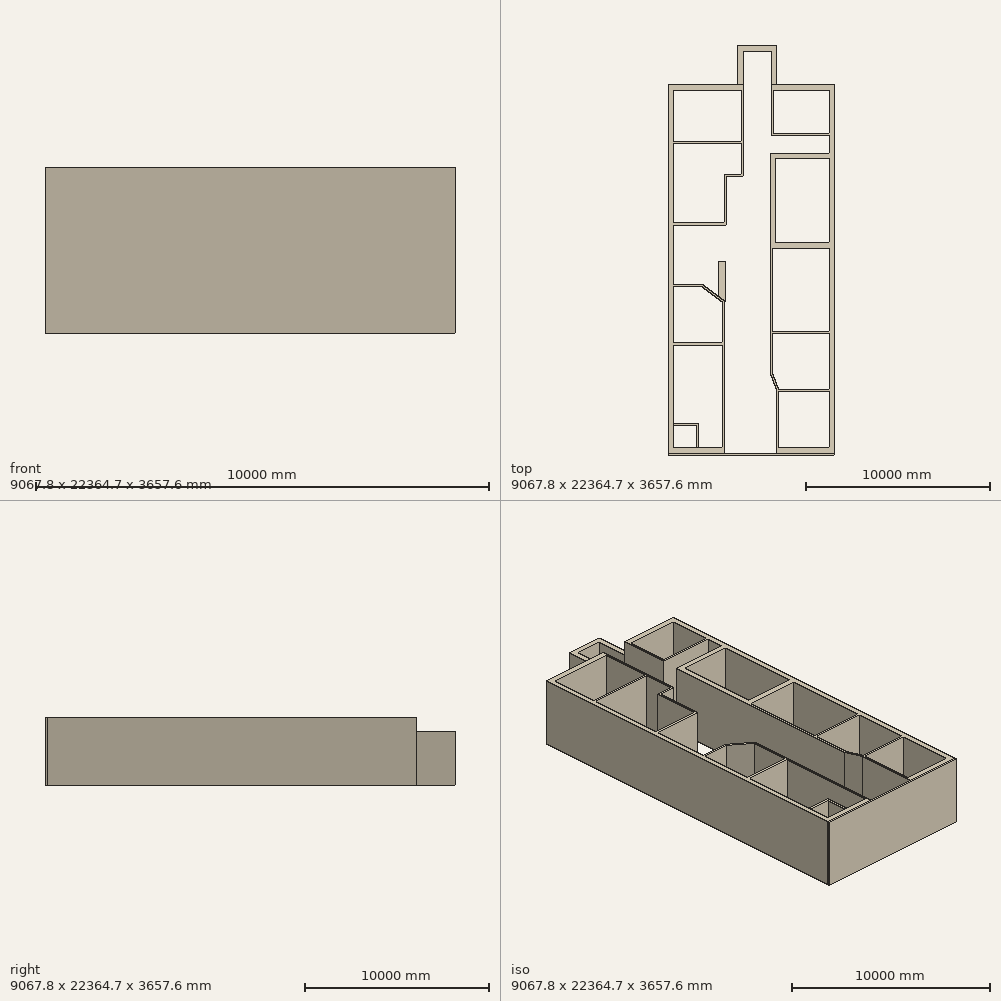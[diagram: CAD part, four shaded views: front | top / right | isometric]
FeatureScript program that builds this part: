
annotation { "Feature Type Name" : "Feature", "Feature Type Description" : "" }
export const myFeature = defineFeature(function(context is Context, id is Id, definition is map)
    precondition{}
    {
        {
            var Q0;
            Q0=qCreatedBy(makeId("Top.planeOp"),FACE);
            var sketch = newSketch(context, id + "F0", { "sketchPlane" : qUnion([Q0])});
            skLineSegment(sketch, "E0.bottom", {"start": v(1936.55, -1664.77) * mm, "end": v(-806.65, -1664.77) * mm});
            skLineSegment(sketch, "E0.top", {"start": v(1936.55, 1383.23) * mm, "end": v(-806.65, 1383.23) * mm});
            skLineSegment(sketch, "E0.left", {"start": v(1936.55, -1664.77) * mm, "end": v(1936.55, 1383.23) * mm});
            skLineSegment(sketch, "E0.right", {"start": v(-806.65, -1664.77) * mm, "end": v(-806.65, 1383.23) * mm});
            skLineSegment(sketch, "E1.0", {"start": v(-920.95, -1969.57) * mm, "end": v(-920.95, 1476.8) * mm});
            skLineSegment(sketch, "E1.1", {"start": v(1936.55, 1497.53) * mm, "end": v(-806.65, 1497.53) * mm});
            skLineSegment(sketch, "E2.1", {"start": v(2241.35, -1969.57) * mm, "end": v(-920.95, -1969.57) * mm});
            skLineSegment(sketch, "E3.0", {"start": v(1936.55, 4545.53) * mm, "end": v(-1149.55, 4545.53) * mm});
            skLineSegment(sketch, "E4", {"start": v(1936.55, 4545.53) * mm, "end": v(1936.55, 1497.53) * mm});
            skLineSegment(sketch, "E5.0", {"start": v(1936.55, 4659.83) * mm, "end": v(-1149.55, 4659.83) * mm});
            skLineSegment(sketch, "E6", {"start": v(-920.95, -1969.57) * mm, "end": v(-3740.35, -1969.57) * mm});
            skLineSegment(sketch, "E7.0", {"start": v(1936.55, 9536.63) * mm, "end": v(-959.05, 9536.63) * mm});
            skLineSegment(sketch, "E8.0", {"start": v(1936.55, 9231.83) * mm, "end": v(-1149.55, 9231.83) * mm});
            skLineSegment(sketch, "E8.1", {"start": v(-1149.55, 4659.83) * mm, "end": v(-1149.55, 9231.83) * mm});
            skLineSegment(sketch, "E9", {"start": v(1936.55, 4659.83) * mm, "end": v(1936.55, 9231.83) * mm});
            skLineSegment(sketch, "E10", {"start": v(2241.35, 9536.63) * mm, "end": v(2241.35, -1969.57) * mm});
            skLineSegment(sketch, "E11.0", {"start": v(1936.55, 14108.63) * mm, "end": v(-959.05, 14108.63) * mm});
            skLineSegment(sketch, "E12.0", {"start": v(1936.55, 14413.43) * mm, "end": v(-1263.85, 14413.43) * mm});
            skLineSegment(sketch, "E13", {"start": v(2241.35, 9536.63) * mm, "end": v(2241.35, 18147.23) * mm});
            skLineSegment(sketch, "E14", {"start": v(1936.55, 9536.63) * mm, "end": v(1936.55, 14108.63) * mm});
            skLineSegment(sketch, "E15", {"start": v(-1263.85, 14413.43) * mm, "end": v(-1263.85, 2391.2) * mm});
            skLineSegment(sketch, "E16.0", {"start": v(-959.05, 14108.63) * mm, "end": v(-959.05, 9536.63) * mm});
            skLineSegment(sketch, "E17", {"start": v(1936.55, 14413.43) * mm, "end": v(1936.55, 15365.93) * mm});
            skLineSegment(sketch, "E18", {"start": v(1936.55, 15365.93) * mm, "end": v(-1225.75, 15365.93) * mm});
            skLineSegment(sketch, "E19.0", {"start": v(1936.55, 17842.43) * mm, "end": v(-1111.45, 17842.43) * mm});
            skLineSegment(sketch, "E20", {"start": v(1936.55, 15480.23) * mm, "end": v(1936.55, 17842.43) * mm});
            skLineSegment(sketch, "E21.0", {"start": v(2241.35, 18147.23) * mm, "end": v(-1225.75, 18147.23) * mm});
            skLineSegment(sketch, "E22.0", {"start": v(-1111.45, 17842.43) * mm, "end": v(-1111.45, 15480.23) * mm});
            skLineSegment(sketch, "E23", {"start": v(-1111.45, 15480.23) * mm, "end": v(1936.55, 15480.23) * mm});
            skLineSegment(sketch, "E24", {"start": v(-1225.75, 15365.93) * mm, "end": v(-1225.75, 18147.23) * mm});
            skLineSegment(sketch, "E25.0", {"start": v(-2749.75, 13118.03) * mm, "end": v(-2749.75, 18147.23) * mm});
            skLineSegment(sketch, "E26.0", {"start": v(-2864.05, 15061.13) * mm, "end": v(-2864.05, 17842.43) * mm});
            skLineSegment(sketch, "E27.0", {"start": v(-6521.65, 15061.13) * mm, "end": v(-6521.65, 17842.43) * mm});
            skLineSegment(sketch, "E28", {"start": v(-2749.75, 18147.23) * mm, "end": v(-6826.45, 18147.23) * mm});
            skLineSegment(sketch, "E29.0", {"start": v(-2864.05, 17842.43) * mm, "end": v(-6521.65, 17842.43) * mm});
            skLineSegment(sketch, "E30.0", {"start": v(-6826.45, -1969.57) * mm, "end": v(-6826.45, 18147.23) * mm});
            skLineSegment(sketch, "E31.0", {"start": v(-2864.05, 15061.13) * mm, "end": v(-6521.65, 15061.13) * mm});
            skLineSegment(sketch, "E32.0", {"start": v(-2864.05, 14946.83) * mm, "end": v(-6521.65, 14946.83) * mm});
            skLineSegment(sketch, "E33.0", {"start": v(-3778.45, 10603.43) * mm, "end": v(-6521.65, 10603.43) * mm});
            skLineSegment(sketch, "E34", {"start": v(-6521.65, 14946.83) * mm, "end": v(-6521.65, 10603.43) * mm});
            skLineSegment(sketch, "E35.0", {"start": v(-3778.45, 13232.33) * mm, "end": v(-3778.45, 10603.43) * mm});
            skLineSegment(sketch, "E36.0", {"start": v(-2749.75, 13118.03) * mm, "end": v(-3664.15, 13118.03) * mm});
            skLineSegment(sketch, "E37", {"start": v(-2864.05, 14946.83) * mm, "end": v(-2864.05, 13232.33) * mm});
            skLineSegment(sketch, "E38.0", {"start": v(-2864.05, 13232.33) * mm, "end": v(-3778.45, 13232.33) * mm});
            skLineSegment(sketch, "E39.0", {"start": v(-3664.15, 13118.03) * mm, "end": v(-3664.15, 10489.13) * mm});
            skLineSegment(sketch, "E40.0", {"start": v(-3664.15, 10489.13) * mm, "end": v(-6521.65, 10489.13) * mm});
            skLineSegment(sketch, "E41.0", {"start": v(-4959.55, 7237.93) * mm, "end": v(-6521.65, 7237.93) * mm});
            skLineSegment(sketch, "E42", {"start": v(-6521.65, 7123.63) * mm, "end": v(-6521.65, -1664.77) * mm});
            skLineSegment(sketch, "E43.0", {"start": v(-4997.65, 7123.63) * mm, "end": v(-6521.65, 7123.63) * mm});
            skLineSegment(sketch, "E44", {"start": v(-1149.55, 2411.93) * mm, "end": v(-1149.55, 4545.53) * mm});
            skLineSegment(sketch, "E45", {"start": v(-6826.45, -1969.57) * mm, "end": v(-3740.35, -1969.57) * mm});
            skLineSegment(sketch, "E46", {"start": v(-6521.65, 10489.13) * mm, "end": v(-6521.65, 7237.93) * mm});
            skLineSegment(sketch, "E47", {"start": v(-3740.35, 6323.53) * mm, "end": v(-3740.35, -1969.57) * mm});
            skLineSegment(sketch, "E48.0", {"start": v(-3854.65, 6266.38) * mm, "end": v(-3854.65, -1664.77) * mm});
            skLineSegment(sketch, "E49", {"start": v(-806.65, 1497.53) * mm, "end": v(-1149.55, 2411.93) * mm});
            skLineSegment(sketch, "E50.0", {"start": v(-920.95, 1476.8) * mm, "end": v(-1263.85, 2391.2) * mm});
            skPoint(sketch, "E51.orphan", {"position": v(-1263.85, 2587.67) * mm});
            skLineSegment(sketch, "E52.0", {"start": v(-6521.65, -1664.77) * mm, "end": v(-3854.65, -1664.77) * mm});
            skLineSegment(sketch, "E53", {"start": v(-2749.75, 18147.23) * mm, "end": v(-1225.75, 18147.23) * mm});
            skLineSegment(sketch, "E54.bottom", {"start": v(-2749.75, 19976.03) * mm, "end": v(-1225.75, 19976.03) * mm});
            skLineSegment(sketch, "E54.left", {"start": v(-2749.75, 19976.03) * mm, "end": v(-2749.75, 18147.23) * mm});
            skLineSegment(sketch, "E54.right", {"start": v(-1225.75, 19976.03) * mm, "end": v(-1225.75, 18147.23) * mm});
            skLineSegment(sketch, "E55.0", {"start": v(-3054.55, 20280.83) * mm, "end": v(-3054.55, 18147.23) * mm});
            skLineSegment(sketch, "E55.1", {"start": v(-3054.55, 20280.83) * mm, "end": v(-920.95, 20280.83) * mm});
            skLineSegment(sketch, "E55.2", {"start": v(-920.95, 20280.83) * mm, "end": v(-920.95, 18147.23) * mm});
            skLineSegment(sketch, "E56.0", {"start": v(-920.95, -1855.27) * mm, "end": v(-3740.35, -1855.27) * mm});
            skLineSegment(sketch, "E57.0", {"start": v(-920.95, -636.07) * mm, "end": v(-3740.35, -636.07) * mm});
            skLineSegment(sketch, "E58.0", {"start": v(-920.95, -750.37) * mm, "end": v(-3740.35, -750.37) * mm});
            skLineSegment(sketch, "E59", {"start": v(-3740.35, 6323.53) * mm, "end": v(-4959.55, 7237.93) * mm});
            skLineSegment(sketch, "E60.0", {"start": v(-3854.65, 6266.38) * mm, "end": v(-4997.65, 7123.63) * mm});
            skSolve(sketch);
        }
        {
            var Q0;
            {var subQ1=sQuery(id+"F0.wireOp",EDGE,"E25.0");Q0=makeQuery(id+"F0.imprint","IMPRINT",FACE,{"disambiguationData":[TD([[makeQuery(id+"F0.imprint","IMPRINT",EDGE,{"derivedFrom":subQ1}),1.0]])]});}
            var Q1;
            Q1=makeQuery(id+"F0.imprint","IMPRINT",FACE,{"disambiguationData":[TD([[makeQuery(id+"F0.imprint","IMPRINT",EDGE,{"derivedFrom":sQuery(id+"F0.wireOp",EDGE,"E0.bottom")}),1.0]])]});
            extrude(context, id + "F1", {"entities" : qUnion([Q0, Q1]), "depth" : 3657.6 * mm, "offsetDistance" : 25.4 * mm});
        }
        {
            var Q0;
            Q0=makeQuery(id+"F0.imprint","IMPRINT",FACE,{"disambiguationData":[TD([[makeQuery(id+"F0.imprint","IMPRINT",EDGE,{"derivedFrom":sQuery(id+"F0.wireOp",EDGE,"E54.bottom")}),1.0]])]});
            extrude(context, id + "F2", {"entities" : qUnion([Q0]), "depth" : 2895.6 * mm, "offsetDistance" : 25.4 * mm});
        }
        {
            var Q0;
            Q0=makeQuery(id+"F1.opExtrude","SWEPT_FACE",FACE,{"disambiguationData":[OSD([sQuery(id+"F0.wireOp",EDGE,"E45")])]});
            var sketch = newSketch(context, id + "F3", { "sketchPlane" : qUnion([Q0])});
            skLineSegment(sketch, "E61.bottom", {"start": v(-6826.45, 3657.6) * mm, "end": v(2241.35, 3657.6) * mm});
            skLineSegment(sketch, "E61.top", {"start": v(-6826.45, 0) * mm, "end": v(2241.35, 0) * mm});
            skLineSegment(sketch, "E61.left", {"start": v(-6826.45, 3657.6) * mm, "end": v(-6826.45, 0) * mm});
            skLineSegment(sketch, "E61.right", {"start": v(2241.35, 3657.6) * mm, "end": v(2241.35, 0) * mm});
            skSolve(sketch);
        }
        {
            var Q0;
            Q0 = qSketchRegion(id + "F3", true);
            extrude(context, id + "F4", {"entities" : qUnion([Q0]), "depth" : 114.3 * mm, "offsetDistance" : 25.4 * mm});
        }
        {
            var Q0;
            Q0=makeQuery(id+"F0.imprint","IMPRINT",FACE,{"disambiguationData":[TD([[makeQuery(id+"F0.imprint","IMPRINT",EDGE,{"derivedFrom":sQuery(id+"F0.wireOp",EDGE,"E42")}),1.0]])]});
            var sketch = newSketch(context, id + "F5", { "sketchPlane" : qUnion([Q0])});
            skLineSegment(sketch, "E62.0", {"start": v(-3854.65, 4075.63) * mm, "end": v(-6521.65, 4075.63) * mm});
            skLineSegment(sketch, "E63.0", {"start": v(-3854.65, 3923.23) * mm, "end": v(-6521.65, 3923.23) * mm});
            skLineSegment(sketch, "E64", {"start": v(-3854.65, 4075.63) * mm, "end": v(-3854.65, 3923.23) * mm});
            skLineSegment(sketch, "E65", {"start": v(-3854.65, 2704.03) * mm, "end": v(-3854.65, 2589.73) * mm});
            skLineSegment(sketch, "E66", {"start": v(-6521.65, 4075.63) * mm, "end": v(-6521.65, 3923.23) * mm});
            skSolve(sketch);
        }
        {
            var Q0;
            Q0 = qSketchRegion(id + "F5", true);
            extrude(context, id + "F6", {"entities" : qUnion([Q0]), "operationType" : NewBodyOperationType.ADD, "depth" : 3657.6 * mm, "offsetDistance" : 25.4 * mm});
        }
        {
            var Q0;
            Q0=makeQuery(id+"F0.imprint","IMPRINT",FACE,{"disambiguationData":[TD([[makeQuery(id+"F0.imprint","IMPRINT",EDGE,{"derivedFrom":sQuery(id+"F0.wireOp",EDGE,"E42")}),1.0]])]});
            var sketch = newSketch(context, id + "F7", { "sketchPlane" : qUnion([Q0])});
            skLineSegment(sketch, "E67.bottom", {"start": v(-6521.65, -445.57) * mm, "end": v(-5302.45, -445.57) * mm});
            skLineSegment(sketch, "E67.right", {"start": v(-5302.45, -445.57) * mm, "end": v(-5302.45, -1664.77) * mm});
            skLineSegment(sketch, "E68.0", {"start": v(-5188.15, -331.27) * mm, "end": v(-5188.15, -1664.77) * mm});
            skLineSegment(sketch, "E68.1", {"start": v(-6521.65, -331.27) * mm, "end": v(-5188.15, -331.27) * mm});
            skLineSegment(sketch, "E69", {"start": v(-6521.65, -331.27) * mm, "end": v(-6521.65, -445.57) * mm});
            skLineSegment(sketch, "E70", {"start": v(-5188.15, -1664.77) * mm, "end": v(-5302.45, -1664.77) * mm});
            skSolve(sketch);
        }
        {
            var Q0;
            Q0 = qSketchRegion(id + "F7", true);
            extrude(context, id + "F8", {"entities" : qUnion([Q0]), "depth" : 3657.6 * mm, "offsetDistance" : 25.4 * mm});
        }
        {
            var Q0;
            Q0=makeQuery(id+"F8.opExtrude","SWEPT_FACE",FACE,{"disambiguationData":[OSD([sQuery(id+"F7.wireOp",EDGE,"E68.0")])]});
            var sketch = newSketch(context, id + "F9", { "sketchPlane" : qUnion([Q0])});
            skLineSegment(sketch, "E71.0", {"start": v(-648.77, 2032) * mm, "end": v(-1461.57, 2032) * mm});
            skLineSegment(sketch, "E72.0", {"start": v(-648.77, 2032) * mm, "end": v(-648.77, 0) * mm});
            skLineSegment(sketch, "E73.0", {"start": v(-1461.57, 2032) * mm, "end": v(-1461.57, 0) * mm});
            skLineSegment(sketch, "E74", {"start": v(-648.77, 0) * mm, "end": v(-1461.57, 0) * mm});
            skSolve(sketch);
        }
        {
            var Q0;
            Q0=makeQuery(id+"F9.imprint","IMPRINT",FACE,{"disambiguationData":[TD([[makeQuery(id+"F9.imprint","IMPRINT",EDGE,{"derivedFrom":sQuery(id+"F9.wireOp",EDGE,"E71.0")}),1.0]])]});
            extrude(context, id + "F10", {"entities" : qUnion([Q0]), "operationType" : NewBodyOperationType.REMOVE, "oppositeDirection" : true, "depth" : 114.3 * mm, "offsetDistance" : 25.4 * mm});
        }
        {
            var Q0;
            Q0=makeQuery(id+"F6.opExtrude","SWEPT_FACE",FACE,{"disambiguationData":[OSD([sQuery(id+"F5.wireOp",EDGE,"E63.0")])]});
            var sketch = newSketch(context, id + "F11", { "sketchPlane" : qUnion([Q0])});
            skLineSegment(sketch, "E75.0", {"start": v(-5797.75, 914.4) * mm, "end": v(-4578.55, 914.4) * mm});
            skLineSegment(sketch, "E75.1", {"start": v(-5797.75, 1828.8) * mm, "end": v(-5797.75, 914.4) * mm});
            skLineSegment(sketch, "E75.2", {"start": v(-4578.55, 1828.8) * mm, "end": v(-5797.75, 1828.8) * mm});
            skLineSegment(sketch, "E75.3", {"start": v(-4578.55, 914.4) * mm, "end": v(-4578.55, 1828.8) * mm});
            skSolve(sketch);
        }
        {
            var Q0;
            Q0 = qSketchRegion(id + "F11", true);
            extrude(context, id + "F12", {"entities" : qUnion([Q0]), "operationType" : NewBodyOperationType.REMOVE, "oppositeDirection" : true, "depth" : 152.4 * mm, "offsetDistance" : 25.4 * mm});
        }
        {
            var Q0;
            Q0=makeQuery(id+"F0.imprint","IMPRINT",FACE,{"disambiguationData":[TD([[makeQuery(id+"F0.imprint","IMPRINT",EDGE,{"derivedFrom":sQuery(id+"F0.wireOp",EDGE,"E12.0")}),-1.0]])]});
            var sketch = newSketch(context, id + "F13", { "sketchPlane" : qUnion([Q0])});
            skLineSegment(sketch, "E76.0", {"start": v(-3746.7, 6323.53) * mm, "end": v(-3746.7, -1969.57) * mm});
            skLineSegment(sketch, "E77", {"start": v(-3746.7, 6323.53) * mm, "end": v(-3746.7, 8457.13) * mm});
            skLineSegment(sketch, "E78.0", {"start": v(-4051.5, 6556.9) * mm, "end": v(-4051.5, 8457.13) * mm});
            skLineSegment(sketch, "E79.0", {"start": v(-3740.35, 6323.53) * mm, "end": v(-4051.5, 6556.9) * mm});
            skLineSegment(sketch, "E80", {"start": v(-4051.5, 8457.13) * mm, "end": v(-3746.7, 8457.13) * mm});
            skSolve(sketch);
        }
        {
            var Q0;
            {var subQ4=sQuery(id+"F13.wireOp",EDGE,"E78.0");Q0=makeQuery(id+"F13.imprint","IMPRINT",FACE,{"disambiguationData":[TD([[makeQuery(id+"F13.imprint","IMPRINT",EDGE,{"derivedFrom":subQ4}),-1.0]])]});}
            extrude(context, id + "F14", {"entities" : qUnion([Q0]), "operationType" : NewBodyOperationType.ADD, "depth" : 914.4 * mm, "offsetDistance" : 25.4 * mm});
        }
        {
            var Q0;
            Q0=makeQuery(id+"F14.opExtrude","CAP_FACE",FACE,{"disambiguationData":[OSD([sQuery(id+"F13.wireOp",EDGE,"E77"),sQuery(id+"F13.wireOp",EDGE,"E78.0"),sQuery(id+"F13.wireOp",EDGE,"E79.0"),sQuery(id+"F13.wireOp",EDGE,"E80")])],"isStart":false});
            var sketch = newSketch(context, id + "F15", { "sketchPlane" : qUnion([Q0])});
            skLineSegment(sketch, "E81.0", {"start": v(-4089.6, 8495.23) * mm, "end": v(-4089.6, 6537.84) * mm});
            skLineSegment(sketch, "E81.1", {"start": v(-3708.6, 8495.23) * mm, "end": v(-4089.6, 8495.23) * mm});
            skLineSegment(sketch, "E81.2", {"start": v(-3708.6, 6252.1) * mm, "end": v(-3708.6, 8495.23) * mm});
            skLineSegment(sketch, "E81.3", {"start": v(-4089.6, 6537.84) * mm, "end": v(-3708.6, 6252.1) * mm});
            skSolve(sketch);
        }
        {
            var Q0;
            Q0 = qSketchRegion(id + "F15", true);
            extrude(context, id + "F16", {"entities" : qUnion([Q0]), "operationType" : NewBodyOperationType.ADD, "depth" : 38.1 * mm, "offsetDistance" : 25.4 * mm});
        }
    });
